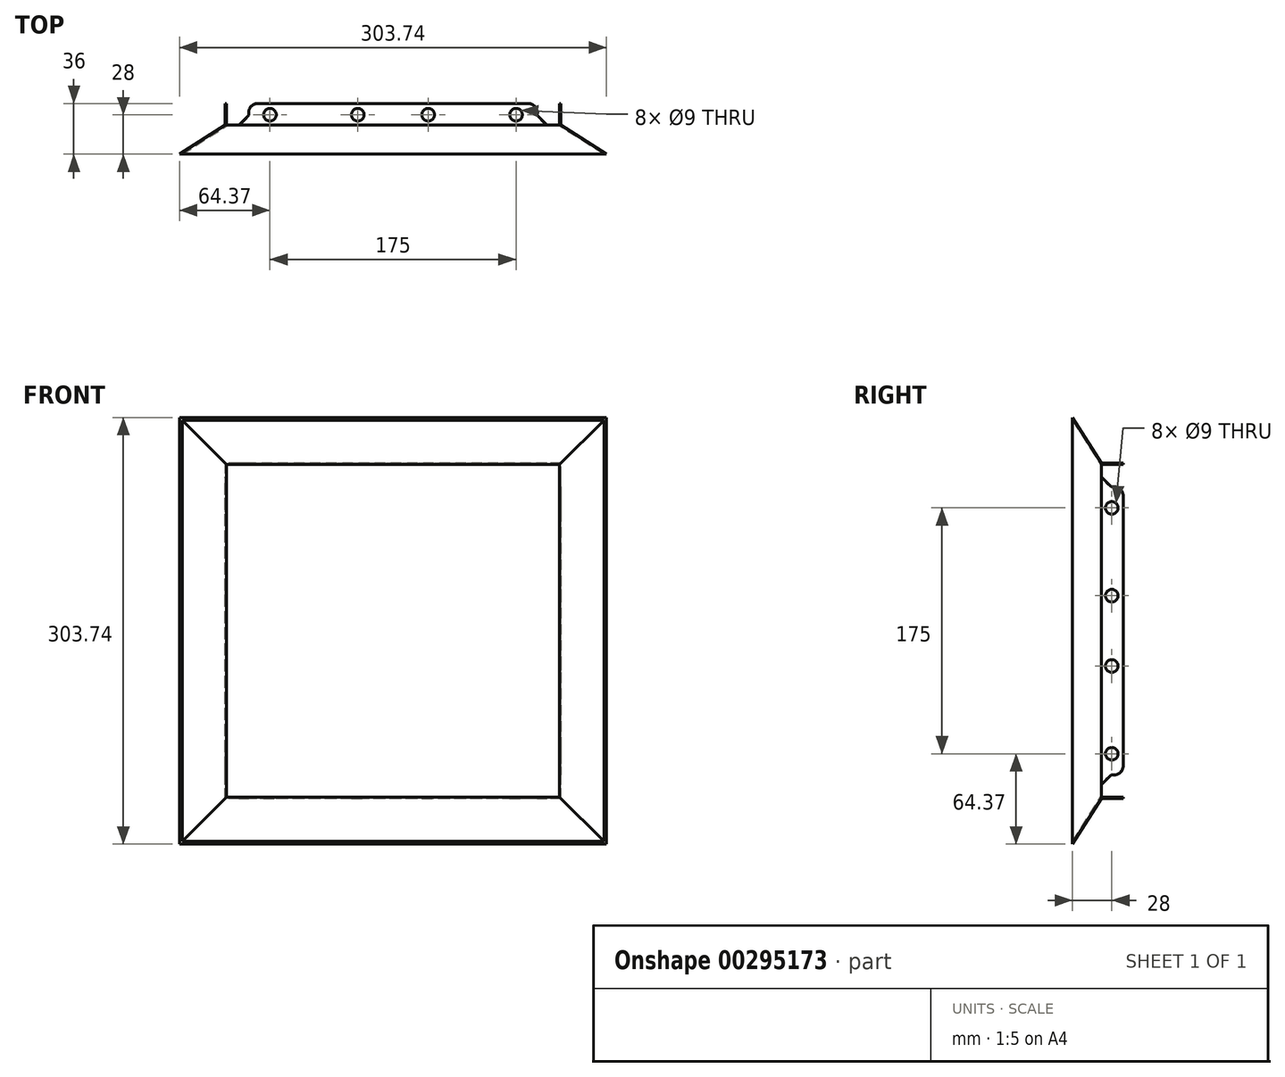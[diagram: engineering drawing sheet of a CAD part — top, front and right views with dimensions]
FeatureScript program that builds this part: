
annotation { "Feature Type Name" : "Feature", "Feature Type Description" : "" }
export const myFeature = defineFeature(function(context is Context, id is Id, definition is map)
    precondition{}
    {
        {
            var Q0;
            Q0=qCreatedBy(makeId("Front.planeOp"),FACE);
            var sketch = newSketch(context, id + "F0", { "sketchPlane" : qUnion([Q0])});
            skLineSegment(sketch, "E0.bottom", {"start": v(155, 155) * mm, "end": v(-155, 155) * mm});
            skLineSegment(sketch, "E0.top", {"start": v(155, -155) * mm, "end": v(-155, -155) * mm});
            skLineSegment(sketch, "E0.left", {"start": v(155, 155) * mm, "end": v(155, -155) * mm});
            skLineSegment(sketch, "E0.right", {"start": v(-155, 155) * mm, "end": v(-155, -155) * mm});
            skPoint(sketch, "E0.middle", {"position": v(0, 0) * mm});
            skLineSegment(sketch, "E1.bottom", {"start": v(-150, 150) * mm, "end": v(150, 150) * mm});
            skLineSegment(sketch, "E1.top", {"start": v(-150, -150) * mm, "end": v(150, -150) * mm});
            skLineSegment(sketch, "E1.left", {"start": v(-150, 150) * mm, "end": v(-150, -150) * mm});
            skLineSegment(sketch, "E1.right", {"start": v(150, 150) * mm, "end": v(150, -150) * mm});
            skSolve(sketch);
        }
        {
            var Q0;
            Q0=qCreatedBy(makeId("Front.planeOp"),FACE);
            cPlane(context, id + "F1", {"entities" : qUnion([Q0]), "cplaneType" : CPlaneType.OFFSET, "offset" : 20 * mm, "oppositeDirection" : true, "width" : 150 * mm, "height" : 150 * mm});
        }
        {
            var Q0;
            Q0=qCreatedBy(id+"F1.planeOp",FACE);
            var sketch = newSketch(context, id + "F2", { "sketchPlane" : qUnion([Q0])});
            skLineSegment(sketch, "E2.bottom", {"start": v(118.5, 118.5) * mm, "end": v(-118.5, 118.5) * mm});
            skLineSegment(sketch, "E2.top", {"start": v(118.5, -118.5) * mm, "end": v(-118.5, -118.5) * mm});
            skLineSegment(sketch, "E2.left", {"start": v(118.5, 118.5) * mm, "end": v(118.5, -118.5) * mm});
            skLineSegment(sketch, "E2.right", {"start": v(-118.5, 118.5) * mm, "end": v(-118.5, -118.5) * mm});
            skPoint(sketch, "E2.middle", {"position": v(0, 0) * mm});
            skSolve(sketch);
        }
        {
            var Q0;
            Q0=makeQuery(id+"F0.imprint","IMPRINT",FACE,{"disambiguationData":[TD([[makeQuery(id+"F0.imprint","IMPRINT",EDGE,{"derivedFrom":sQuery(id+"F0.wireOp",EDGE,"E1.bottom")}),-1.0]])]});
            var Q1;
            Q1=makeQuery(id+"F2.imprint","IMPRINT",FACE,{"disambiguationData":[TD([[makeQuery(id+"F2.imprint","IMPRINT",EDGE,{"derivedFrom":sQuery(id+"F2.wireOp",EDGE,"E2.bottom")}),1.0]])]});
            loft(context, id + "F3", {"sheetProfilesArray" : [{ "sheetProfileEntities" : qUnion([Q0]) }, { "sheetProfileEntities" : qUnion([Q1]) }]});
        }
        {
            var Q0;
            Q0=qCreatedBy(id+"F1.planeOp",FACE);
            cPlane(context, id + "F4", {"entities" : qUnion([Q0]), "cplaneType" : CPlaneType.OFFSET, "offset" : 16 * mm, "oppositeDirection" : true, "width" : 150 * mm, "height" : 150 * mm});
        }
        {
            var Q0;
            Q0=qCreatedBy(id+"F4.planeOp",FACE);
            var sketch = newSketch(context, id + "F5", { "sketchPlane" : qUnion([Q0])});
            skLineSegment(sketch, "E3.0.0", {"start": v(118.5, -118.5) * mm, "end": v(-118.5, -118.5) * mm});
            skLineSegment(sketch, "E3.0.1", {"start": v(-118.5, -118.5) * mm, "end": v(-118.5, 118.5) * mm});
            skLineSegment(sketch, "E3.0.2", {"start": v(-118.5, 118.5) * mm, "end": v(118.5, 118.5) * mm});
            skLineSegment(sketch, "E3.0.3", {"start": v(118.5, 118.5) * mm, "end": v(118.5, -118.5) * mm});
            skSolve(sketch);
        }
        {
            var Q1;
            Q1=makeQuery(id+"F5.imprint","IMPRINT",FACE,{"disambiguationData":[TD([[makeQuery(id+"F5.imprint","IMPRINT",EDGE,{"derivedFrom":sQuery(id+"F5.wireOp",EDGE,"E3.0.0")}),-1.0]])]});
            var Q2;
            Q2=makeQuery(id+"F3.opLoft","CAP_FACE",FACE,{"disambiguationData":[OSD([makeQuery(id+"F2.imprint","IMPRINT",FACE,{"disambiguationData":[TD([[makeQuery(id+"F2.imprint","IMPRINT",EDGE,{"derivedFrom":sQuery(id+"F2.wireOp",EDGE,"E2.bottom")}),1.0]])]})])],"isStart":true});
            loft(context, id + "F6", {"operationType" : NewBodyOperationType.ADD, "sheetProfilesArray" : [{ "sheetProfileEntities" : qUnion([Q1]) }, { "sheetProfileEntities" : qUnion([Q2]) }]});
        }
        {
            var Q0;
            Q0=makeQuery(id+"F3.opLoft","CAP_FACE",FACE,{"disambiguationData":[OSD([makeQuery(id+"F0.imprint","IMPRINT",FACE,{"disambiguationData":[TD([[makeQuery(id+"F0.imprint","IMPRINT",EDGE,{"derivedFrom":sQuery(id+"F0.wireOp",EDGE,"E1.bottom")}),-1.0]])]})])],"isStart":true});
            var Q1;
            Q1=makeQuery(id+"F6.opLoft","CAP_FACE",FACE,{"disambiguationData":[OSD([makeQuery(id+"F5.imprint","IMPRINT",FACE,{"disambiguationData":[TD([[makeQuery(id+"F5.imprint","IMPRINT",EDGE,{"derivedFrom":sQuery(id+"F5.wireOp",EDGE,"E3.0.0")}),-1.0]])]})])],"isStart":true});
            shell(context, id + "F7", {"entities" : qUnion([Q0, Q1]), "thickness" : 1 * mm, "oppositeDirection" : true});
        }
        {
            var Q0;
            Q0=makeQuery(id+"F6.opLoft","SWEPT_FACE",FACE,{"disambiguationData":[OSD([sQuery(id+"F2.wireOp",EDGE,"E2.bottom"),sQuery(id+"F2.wireOp",EDGE,"E2.top"),sQuery(id+"F2.wireOp",EDGE,"E2.right"),sQuery(id+"F5.wireOp",EDGE,"E3.0.0"),sQuery(id+"F5.wireOp",EDGE,"E3.0.1"),sQuery(id+"F5.wireOp",EDGE,"E3.0.2")])]});
            var sketch = newSketch(context, id + "F8", { "sketchPlane" : qUnion([Q0])});
            skLineSegment(sketch, "E4", {"start": v(-20.55, 119.5) * mm, "end": v(-20.55, 109.5) * mm});
            skLineSegment(sketch, "E5", {"start": v(-20.55, 109.5) * mm, "end": v(-27.62, 102.43) * mm});
            skArc(sketch, "E6", {"start": v(-27.62, 102.43) * mm, "mid": v(-33.79, 101.03) * mm, "end": v(-36, 95.1) * mm});
            skLineSegment(sketch, "E7", {"start": v(-20.55, 119.5) * mm, "end": v(-36, 119.5) * mm});
            skLineSegment(sketch, "E8", {"start": v(-36, 119.5) * mm, "end": v(-36, 95.1) * mm});
            skLineSegment(sketch, "E9.MirrorCS", {"start": v(-20.55, -119.5) * mm, "end": v(-36, -119.5) * mm});
            skArc(sketch, "E10.MirrorCS", {"start": v(-27.62, -102.43) * mm, "mid": v(-33.79, -101.03) * mm, "end": v(-36, -95.1) * mm});
            skLineSegment(sketch, "E11.MirrorCS", {"start": v(-20.55, -119.5) * mm, "end": v(-20.55, -109.5) * mm});
            skLineSegment(sketch, "E12.MirrorCS", {"start": v(-20.55, -109.5) * mm, "end": v(-27.62, -102.43) * mm});
            skLineSegment(sketch, "E13.MirrorCS", {"start": v(-36, -119.5) * mm, "end": v(-36, -95.1) * mm});
            skSolve(sketch);
        }
        {
            var Q0;
            Q0=makeQuery(id+"F8.imprint","IMPRINT",FACE,{"disambiguationData":[TD([[makeQuery(id+"F8.imprint","IMPRINT",EDGE,{"derivedFrom":sQuery(id+"F8.wireOp",EDGE,"E4")}),1.0]])]});
            var Q1;
            Q1=sQuery(id+"F8.wireOp",EDGE,"E7");
            revolve(context, id + "F9", {"operationType" : NewBodyOperationType.REMOVE, "entities" : qUnion([Q0]), "axis" : qUnion([Q1]), "revolveType" : RevolveType.FULL, "oppositeDirection" : true});
        }
        {
            var Q0;
            {var subQ4=sQuery(id+"F8.wireOp",EDGE,"E9.MirrorCS");Q0=makeQuery(id+"F8.imprint","IMPRINT",FACE,{"disambiguationData":[TD([[makeQuery(id+"F8.imprint","IMPRINT",EDGE,{"derivedFrom":subQ4}),1.0]])]});}
            var Q1;
            Q1=sQuery(id+"F8.wireOp",EDGE,"E9.MirrorCS");
            revolve(context, id + "F10", {"operationType" : NewBodyOperationType.REMOVE, "entities" : qUnion([Q0]), "axis" : qUnion([Q1]), "revolveType" : RevolveType.FULL, "oppositeDirection" : true});
        }
        {
            var Q0;
            Q0=makeQuery(id+"F6.opLoft","SWEPT_FACE",FACE,{"disambiguationData":[OSD([sQuery(id+"F2.wireOp",EDGE,"E2.bottom"),sQuery(id+"F2.wireOp",EDGE,"E2.top"),sQuery(id+"F2.wireOp",EDGE,"E2.left"),sQuery(id+"F5.wireOp",EDGE,"E3.0.0"),sQuery(id+"F5.wireOp",EDGE,"E3.0.2"),sQuery(id+"F5.wireOp",EDGE,"E3.0.3")])]});
            var sketch = newSketch(context, id + "F11", { "sketchPlane" : qUnion([Q0])});
            skLineSegment(sketch, "E14.0", {"start": v(20.55, -109.5) * mm, "end": v(27.62, -102.43) * mm});
            skArc(sketch, "E15.0", {"start": v(27.62, -102.43) * mm, "mid": v(33.79, -101.03) * mm, "end": v(36, -95.1) * mm});
            skLineSegment(sketch, "E16.0", {"start": v(20.55, -119.5) * mm, "end": v(20.55, -109.5) * mm});
            skLineSegment(sketch, "E17.0", {"start": v(20.55, -119.5) * mm, "end": v(36, -119.5) * mm});
            skLineSegment(sketch, "E18.0", {"start": v(36, -119.5) * mm, "end": v(36, -95.1) * mm});
            skLineSegment(sketch, "E19.MirrorCS", {"start": v(20.55, 119.5) * mm, "end": v(20.55, 109.5) * mm});
            skLineSegment(sketch, "E20.MirrorCS", {"start": v(20.55, 119.5) * mm, "end": v(36, 119.5) * mm});
            skLineSegment(sketch, "E21.MirrorCS", {"start": v(20.55, 109.5) * mm, "end": v(27.62, 102.43) * mm});
            skLineSegment(sketch, "E22.MirrorCS", {"start": v(36, 119.5) * mm, "end": v(36, 95.1) * mm});
            skArc(sketch, "E23.MirrorCS", {"start": v(27.62, 102.43) * mm, "mid": v(33.79, 101.03) * mm, "end": v(36, 95.1) * mm});
            skSolve(sketch);
        }
        {
            var Q0;
            {var subQ2=sQuery(id+"F11.wireOp",EDGE,"E14.0");Q0=makeQuery(id+"F11.imprint","IMPRINT",FACE,{"disambiguationData":[TD([[makeQuery(id+"F11.imprint","IMPRINT",EDGE,{"derivedFrom":subQ2}),-1.0]])]});}
            var Q1;
            Q1=sQuery(id+"F11.wireOp",EDGE,"E17.0");
            revolve(context, id + "F12", {"operationType" : NewBodyOperationType.REMOVE, "entities" : qUnion([Q0]), "axis" : qUnion([Q1]), "revolveType" : RevolveType.FULL, "oppositeDirection" : true});
        }
        {
            var Q0;
            Q0=makeQuery(id+"F11.imprint","IMPRINT",FACE,{"disambiguationData":[TD([[makeQuery(id+"F11.imprint","IMPRINT",EDGE,{"derivedFrom":sQuery(id+"F11.wireOp",EDGE,"E19.MirrorCS")}),1.0]])]});
            var Q1;
            Q1=sQuery(id+"F11.wireOp",EDGE,"E20.MirrorCS");
            revolve(context, id + "F13", {"operationType" : NewBodyOperationType.REMOVE, "entities" : qUnion([Q0]), "axis" : qUnion([Q1]), "revolveType" : RevolveType.FULL, "oppositeDirection" : true});
        }
        {
            var Q0;
            Q0=makeQuery(id+"F6.opLoft","SWEPT_FACE",FACE,{"disambiguationData":[OSD([sQuery(id+"F2.wireOp",EDGE,"E2.top"),sQuery(id+"F2.wireOp",EDGE,"E2.left"),sQuery(id+"F2.wireOp",EDGE,"E2.right"),sQuery(id+"F5.wireOp",EDGE,"E3.0.0"),sQuery(id+"F5.wireOp",EDGE,"E3.0.1"),sQuery(id+"F5.wireOp",EDGE,"E3.0.3")])]});
            var sketch = newSketch(context, id + "F14", { "sketchPlane" : qUnion([Q0])});
            skCircle(sketch, "E24", {"center": v(-25, -28) * mm, "radius": 4.5 * mm});
            skCircle(sketch, "E25", {"center": v(25, -28) * mm, "radius": 4.5 * mm});
            skCircle(sketch, "E26", {"center": v(-87.5, -28) * mm, "radius": 4.5 * mm});
            skCircle(sketch, "E27", {"center": v(87.5, -28) * mm, "radius": 4.5 * mm});
            skSolve(sketch);
        }
        {
            var Q0;
            Q0=qSketchRegion(id+"F14",true);
            extrude(context, id + "F15", {"entities" : qUnion([Q0]), "operationType" : NewBodyOperationType.REMOVE, "endBound" : BoundingType.THROUGH_ALL, "oppositeDirection" : true, "depth" : 25 * mm});
        }
        {
            var Q0;
            Q0=makeQuery(id+"F6.opLoft","SWEPT_FACE",FACE,{"disambiguationData":[OSD([sQuery(id+"F2.wireOp",EDGE,"E2.bottom"),sQuery(id+"F2.wireOp",EDGE,"E2.top"),sQuery(id+"F2.wireOp",EDGE,"E2.right"),sQuery(id+"F5.wireOp",EDGE,"E3.0.0"),sQuery(id+"F5.wireOp",EDGE,"E3.0.1"),sQuery(id+"F5.wireOp",EDGE,"E3.0.2")])]});
            var sketch = newSketch(context, id + "F16", { "sketchPlane" : qUnion([Q0])});
            skCircle(sketch, "E28", {"center": v(-28, 25) * mm, "radius": 4.5 * mm});
            skCircle(sketch, "E29", {"center": v(-28, 87.5) * mm, "radius": 4.5 * mm});
            skCircle(sketch, "E30.MirrorC", {"center": v(-28, -25) * mm, "radius": 4.5 * mm});
            skCircle(sketch, "E31.MirrorC", {"center": v(-28, -87.5) * mm, "radius": 4.5 * mm});
            skSolve(sketch);
        }
        {
            var Q0;
            Q0 = qSketchRegion(id + "F16", true);
            extrude(context, id + "F17", {"entities" : qUnion([Q0]), "operationType" : NewBodyOperationType.REMOVE, "endBound" : BoundingType.THROUGH_ALL, "oppositeDirection" : true, "depth" : 25 * mm});
        }
    });
